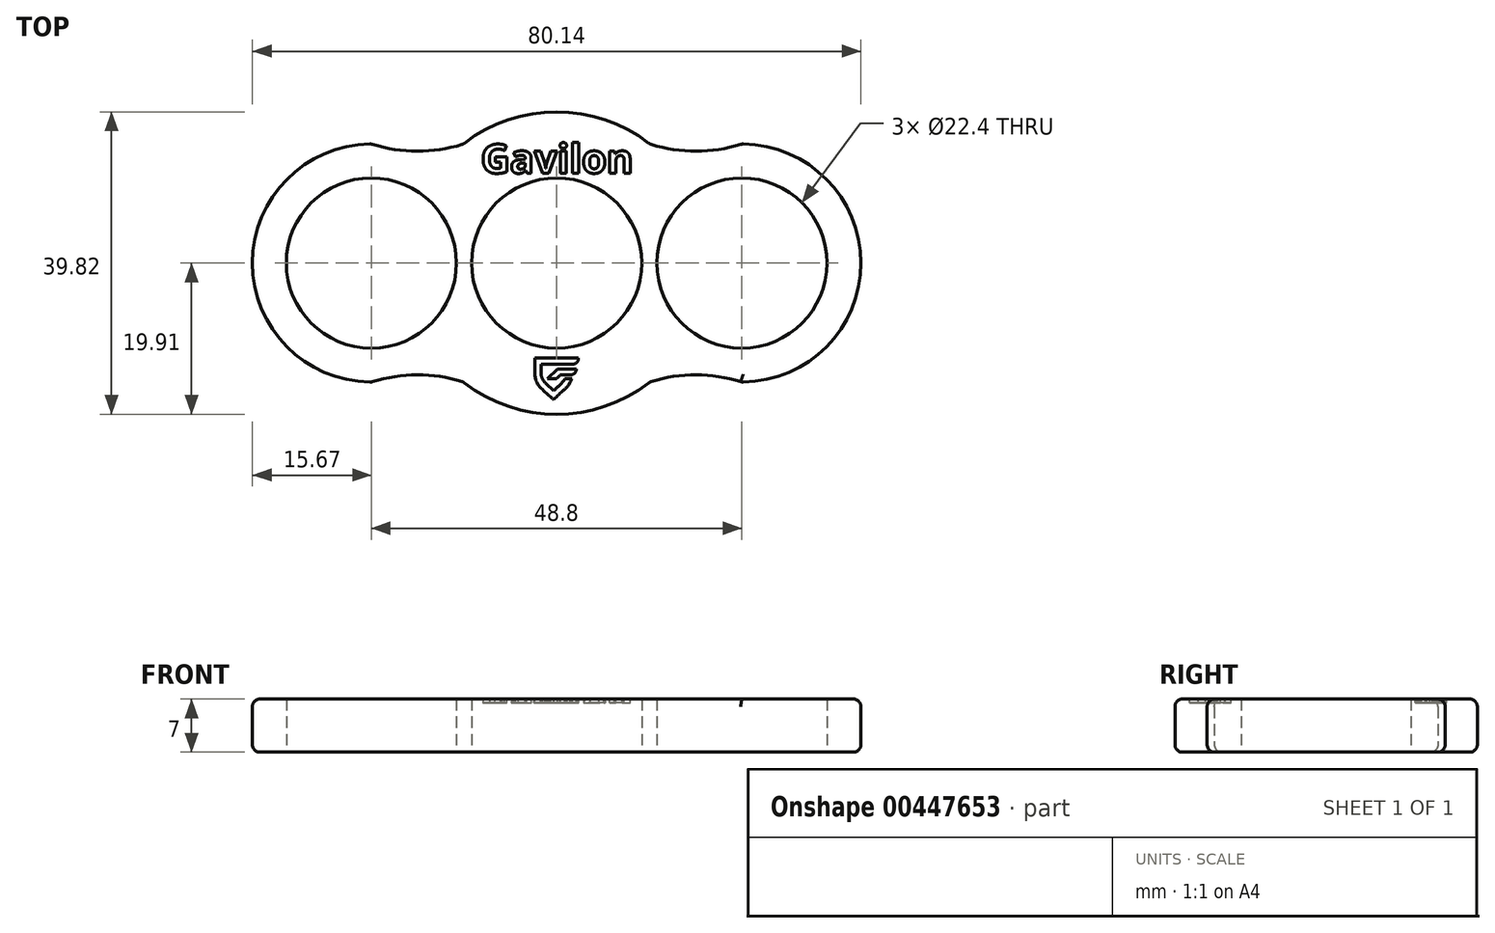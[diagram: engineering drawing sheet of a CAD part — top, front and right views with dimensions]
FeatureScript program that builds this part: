
annotation { "Feature Type Name" : "Feature", "Feature Type Description" : "" }
export const myFeature = defineFeature(function(context is Context, id is Id, definition is map)
    precondition{}
    {
        {
            var Q0;
            Q0=qCreatedBy(makeId("Top.planeOp"),FACE);
            var sketch = newSketch(context, id + "F0", { "sketchPlane" : qUnion([Q0])});
            skCircle(sketch, "E0", {"center": v(0, 0) * mm, "radius": 11.2 * mm});
            skCircle(sketch, "E1", {"center": v(-24.4, 0) * mm, "radius": 11.2 * mm});
            skCircle(sketch, "E2", {"center": v(24.4, 0) * mm, "radius": 11.2 * mm});
            skPoint(sketch, "E3", {"position": v(-13.2, 0) * mm});
            skPoint(sketch, "E4", {"position": v(-11.2, 0) * mm});
            skPoint(sketch, "E5", {"position": v(11.2, 0) * mm});
            skPoint(sketch, "E6", {"position": v(13.2, 0) * mm});
            skLineSegment(sketch, "E7", {"start": v(-13.2, 0) * mm, "end": v(-11.2, 0) * mm, "construction": true});
            skLineSegment(sketch, "E8", {"start": v(11.2, 0) * mm, "end": v(13.2, 0) * mm});
            skArc(sketch, "E9", {"start": v(-24.4, 15.67) * mm, "mid": v(-40.07, 0) * mm, "end": v(-24.4, -15.67) * mm});
            skArc(sketch, "E10", {"start": v(24.4, 15.67) * mm, "mid": v(40.07, 0) * mm, "end": v(24.4, -15.67) * mm});
            skArc(sketch, "E11", {"start": v(12.29, 15.67) * mm, "mid": v(0, 19.91) * mm, "end": v(-12.29, 15.67) * mm});
            skArc(sketch, "E12", {"start": v(12.29, -15.67) * mm, "mid": v(0, -19.91) * mm, "end": v(-12.29, -15.67) * mm});
            skArc(sketch, "E13", {"start": v(-24.4, 15.67) * mm, "mid": v(-18.34, 14.72) * mm, "end": v(-12.29, 15.67) * mm});
            skArc(sketch, "E14", {"start": v(12.29, 15.67) * mm, "mid": v(18.34, 14.72) * mm, "end": v(24.4, 15.67) * mm});
            skArc(sketch, "E15", {"start": v(-12.29, -15.67) * mm, "mid": v(-18.34, -14.72) * mm, "end": v(-24.4, -15.67) * mm});
            skArc(sketch, "E16", {"start": v(24.4, -15.67) * mm, "mid": v(18.34, -14.72) * mm, "end": v(12.29, -15.67) * mm});
            skLineSegment(sketch, "E17", {"start": v(-24.4, -15.67) * mm, "end": v(-12.29, -15.67) * mm, "construction": true});
            skLineSegment(sketch, "E18", {"start": v(12.29, -15.67) * mm, "end": v(24.4, -15.67) * mm, "construction": true});
            skLineSegment(sketch, "E19", {"start": v(12.29, 15.67) * mm, "end": v(24.4, 15.67) * mm, "construction": true});
            skLineSegment(sketch, "E20", {"start": v(-24.4, 15.67) * mm, "end": v(-12.29, 15.67) * mm, "construction": true});
            skLineSegment(sketch, "E21", {"start": v(24.4, 15.67) * mm, "end": v(18.34, 34.6) * mm, "construction": true});
            skLineSegment(sketch, "E22", {"start": v(-24.4, 15.67) * mm, "end": v(-18.34, 34.6) * mm, "construction": true});
            skLineSegment(sketch, "E23", {"start": v(-24.4, -15.67) * mm, "end": v(-18.34, -34.6) * mm, "construction": true});
            skLineSegment(sketch, "E24", {"start": v(24.4, -15.67) * mm, "end": v(18.34, -34.6) * mm, "construction": true});
            skSolve(sketch);
        }
        {
            var Q0;
            Q0=makeQuery(id+"F0.imprint","IMPRINT",FACE,{"disambiguationData":[TD([[makeQuery(id+"F0.imprint","IMPRINT",EDGE,{"derivedFrom":sQuery(id+"F0.wireOp",EDGE,"E0")}),-1.0]])]});
            extrude(context, id + "F1", {"entities" : qUnion([Q0]), "depth" : 7 * mm, "offsetDistance" : 25.4 * mm});
        }
        {
            var Q0;
            Q0=makeQuery(id+"F1.opExtrude","CAP_FACE",FACE,{"disambiguationData":[OSD([sQuery(id+"F0.wireOp",EDGE,"E0"),sQuery(id+"F0.wireOp",EDGE,"E1"),sQuery(id+"F0.wireOp",EDGE,"E2"),sQuery(id+"F0.wireOp",EDGE,"E9"),sQuery(id+"F0.wireOp",EDGE,"E10"),sQuery(id+"F0.wireOp",EDGE,"E11"),sQuery(id+"F0.wireOp",EDGE,"E12"),sQuery(id+"F0.wireOp",EDGE,"E13"),sQuery(id+"F0.wireOp",EDGE,"E14"),sQuery(id+"F0.wireOp",EDGE,"E15"),sQuery(id+"F0.wireOp",EDGE,"E16")])],"isStart":false});
            var sketch = newSketch(context, id + "F2", { "sketchPlane" : qUnion([Q0])});
            skText(sketch, "E25", { "text": "Gavilon", "fontName": "OpenSans-Bold.ttf"});
            skLineSegment(sketch, "E26", {"start": v(-12.29, 15.67) * mm, "end": v(0, 15.64) * mm, "construction": true});
            skLineSegment(sketch, "E27", {"start": v(12.29, 15.67) * mm, "end": v(0, 15.64) * mm, "construction": true});
            const initialGuessF2  = {"E25": [-0.01, 0.01183, 1, 0, 0.00382]};
            skSetInitialGuess(sketch, initialGuessF2);
            skSolve(sketch);
        }
        {
            var Q0;
            Q0=makeQuery(id+"F2.imprint","IMPRINT",FACE,{"disambiguationData":[TD([[makeQuery(id+"F2.imprint","IMPRINT",EDGE,{"derivedFrom":sQuery(id+"F2.wireOp",EDGE,"E25.sketch_text.stroke-0")}),-1.0]])]});
            var Q1;
            Q1=qSketchRegion(id+"F2",true);
            extrude(context, id + "F3", {"entities" : qUnion([Q0, Q1]), "operationType" : NewBodyOperationType.REMOVE, "oppositeDirection" : true, "depth" : .5 * mm, "offsetDistance" : 25.4 * mm, "hasDraft" : true, "draftAngle" : 3 * degree});
        }
        {
            var Q0;
            Q0=makeQuery(id+"F1.opExtrude","SWEPT_FACE",FACE,{"disambiguationData":[OSD([sQuery(id+"F0.wireOp",EDGE,"E9")])]});
            var Q1;
            Q1=makeQuery(id+"F1.opExtrude","SWEPT_FACE",FACE,{"disambiguationData":[OSD([sQuery(id+"F0.wireOp",EDGE,"E15")])]});
            var Q2;
            Q2=makeQuery(id+"F1.opExtrude","SWEPT_FACE",FACE,{"disambiguationData":[OSD([sQuery(id+"F0.wireOp",EDGE,"E12")])]});
            var Q3;
            Q3=makeQuery(id+"F1.opExtrude","SWEPT_FACE",FACE,{"disambiguationData":[OSD([sQuery(id+"F0.wireOp",EDGE,"E16")])]});
            var Q4;
            Q4=makeQuery(id+"F1.opExtrude","SWEPT_FACE",FACE,{"disambiguationData":[OSD([sQuery(id+"F0.wireOp",EDGE,"E10")])]});
            var Q5;
            Q5=makeQuery(id+"F1.opExtrude","SWEPT_FACE",FACE,{"disambiguationData":[OSD([sQuery(id+"F0.wireOp",EDGE,"E14")])]});
            var Q6;
            Q6=makeQuery(id+"F1.opExtrude","SWEPT_FACE",FACE,{"disambiguationData":[OSD([sQuery(id+"F0.wireOp",EDGE,"E11")])]});
            var Q7;
            Q7=makeQuery(id+"F1.opExtrude","SWEPT_FACE",FACE,{"disambiguationData":[OSD([sQuery(id+"F0.wireOp",EDGE,"E13")])]});
            fillet(context, id + "F4", {"entities" : qUnion([Q0, Q1, Q2, Q3, Q4, Q5, Q6, Q7]), "radius" : 1 * mm, "tangentPropagation" : true, "allowEdgeOverflow" : false});
        }
        {
            var Q0;
            {var subQ0=sQuery(id+"F0.wireOp",EDGE,"E16");var subQ1=sQuery(id+"F0.wireOp",EDGE,"E2");var subQ2=sQuery(id+"F0.wireOp",EDGE,"E1");var subQ3=sQuery(id+"F0.wireOp",EDGE,"E9");var subQ4=sQuery(id+"F0.wireOp",EDGE,"E0");var subQ5=sQuery(id+"F0.wireOp",EDGE,"E15");var subQ6=sQuery(id+"F0.wireOp",EDGE,"E10");var subQ7=sQuery(id+"F0.wireOp",EDGE,"E11");var subQ8=sQuery(id+"F0.wireOp",EDGE,"E12");var subQ9=sQuery(id+"F0.wireOp",EDGE,"E13");var subQ10=sQuery(id+"F0.wireOp",EDGE,"E14");Q0=makeQuery(id+"F3.boolean.opBoolean","SPLIT",FACE,{"disambiguationData":[TD([makeQuery(id+"F1.opExtrude","SWEPT_FACE",FACE,{"disambiguationData":[OSD([subQ4])]})])],"derivedFrom":makeQuery(id+"F1.opExtrude","CAP_FACE",FACE,{"disambiguationData":[OSD([subQ4,subQ2,subQ1,subQ3,subQ6,subQ7,subQ8,subQ9,subQ10,subQ5,subQ0])],"isStart":false})});}
            var sketch = newSketch(context, id + "F5", { "sketchPlane" : qUnion([Q0])});
            skLineSegment(sketch, "E28", {"start": v(2.84, -12.52) * mm, "end": v(-2.9, -12.52) * mm});
            skLineSegment(sketch, "E29", {"start": v(-2.9, -12.52) * mm, "end": v(-2.9, -14.58) * mm});
            skFitSpline(sketch, "E30", {"points": [v(-2.9, -14.58) * mm, v(-2.77, -15.3) * mm, v(-2.28, -16.22) * mm, v(-1, -17.46) * mm, v(-0.4, -17.97) * mm], "startDerivative": vector(0.4, -3.4) * mm, "endDerivative": vector(2.41, -2.07) * mm});
            skFitSpline(sketch, "E31", {"points": [v(-0.4, -17.97) * mm, v(0.91, -16.74) * mm, v(1.37, -16.32) * mm, v(1.9, -15.5) * mm, v(2, -15.2) * mm], "startDerivative": vector(4.08, 3.97) * mm, "endDerivative": vector(0.38, 1.65) * mm});
            skLineSegment(sketch, "E32", {"start": v(2, -15.2) * mm, "end": v(1.1, -15.2) * mm});
            skFitSpline(sketch, "E33", {"points": [v(1.1, -15.2) * mm, v(0.8, -15.67) * mm, v(0.26, -16.22) * mm, v(-0.42, -16.81) * mm], "startDerivative": vector(-0.9, -1.62) * mm, "endDerivative": vector(-1.87, -1.6) * mm});
            skLineSegment(sketch, "E34", {"start": v(-0.42, -16.81) * mm, "end": v(-1.4, -15.88) * mm});
            skFitSpline(sketch, "E35", {"points": [v(-1.4, -15.88) * mm, v(-1.63, -15.63) * mm, v(-1.91, -15.15) * mm, v(-2.03, -14.7) * mm, v(-2.06, -13.3) * mm], "startDerivative": vector(-1.27, 1.17) * mm, "endDerivative": vector(0.05, 4.33) * mm});
            skLineSegment(sketch, "E36", {"start": v(-2.06, -13.3) * mm, "end": v(1.97, -13.3) * mm});
            skFitSpline(sketch, "E37", {"points": [v(1.97, -13.3) * mm, v(2.2, -13.3) * mm, v(2.57, -13.17) * mm, v(2.8, -12.9) * mm, v(2.84, -12.72) * mm, v(2.84, -12.52) * mm], "startDerivative": vector(1.16, -0.09) * mm, "endDerivative": vector(-0.05, 1.23) * mm});
            skLineSegment(sketch, "E38", {"start": v(2.61, -13.93) * mm, "end": v(0.12, -13.93) * mm});
            skLineSegment(sketch, "E39", {"start": v(0.12, -13.93) * mm, "end": v(-1.22, -15.24) * mm});
            skLineSegment(sketch, "E40", {"start": v(-1.22, -15.24) * mm, "end": v(-0.32, -15.24) * mm});
            skFitSpline(sketch, "E41", {"points": [v(-0.32, -15.24) * mm, v(-0.1, -15.24) * mm, v(0.45, -14.7) * mm], "startDerivative": vector(0.59, -0.14) * mm, "endDerivative": vector(0.85, 1.36) * mm});
            skLineSegment(sketch, "E42", {"start": v(0.45, -14.7) * mm, "end": v(1.8, -14.7) * mm});
            skFitSpline(sketch, "E43", {"points": [v(1.8, -14.7) * mm, v(2.02, -14.7) * mm, v(2.3, -14.56) * mm, v(2.47, -14.35) * mm, v(2.61, -13.93) * mm], "startDerivative": vector(1.06, -0.15) * mm, "endDerivative": vector(-0.02, 1.47) * mm});
            skSolve(sketch);
        }
        {
            var Q0;
            Q0=makeQuery(id+"F5.imprint","IMPRINT",FACE,{"disambiguationData":[TD([[makeQuery(id+"F5.imprint","IMPRINT",EDGE,{"derivedFrom":sQuery(id+"F5.wireOp",EDGE,"E28")}),1.0]])]});
            var Q1;
            Q1=makeQuery(id+"F5.imprint","IMPRINT",FACE,{"disambiguationData":[TD([[makeQuery(id+"F5.imprint","IMPRINT",EDGE,{"derivedFrom":sQuery(id+"F5.wireOp",EDGE,"E38")}),1.0]])]});
            extrude(context, id + "F6", {"entities" : qUnion([Q0, Q1]), "operationType" : NewBodyOperationType.REMOVE, "oppositeDirection" : true, "depth" : .5 * mm, "offsetDistance" : 25 * mm});
        }
    });
